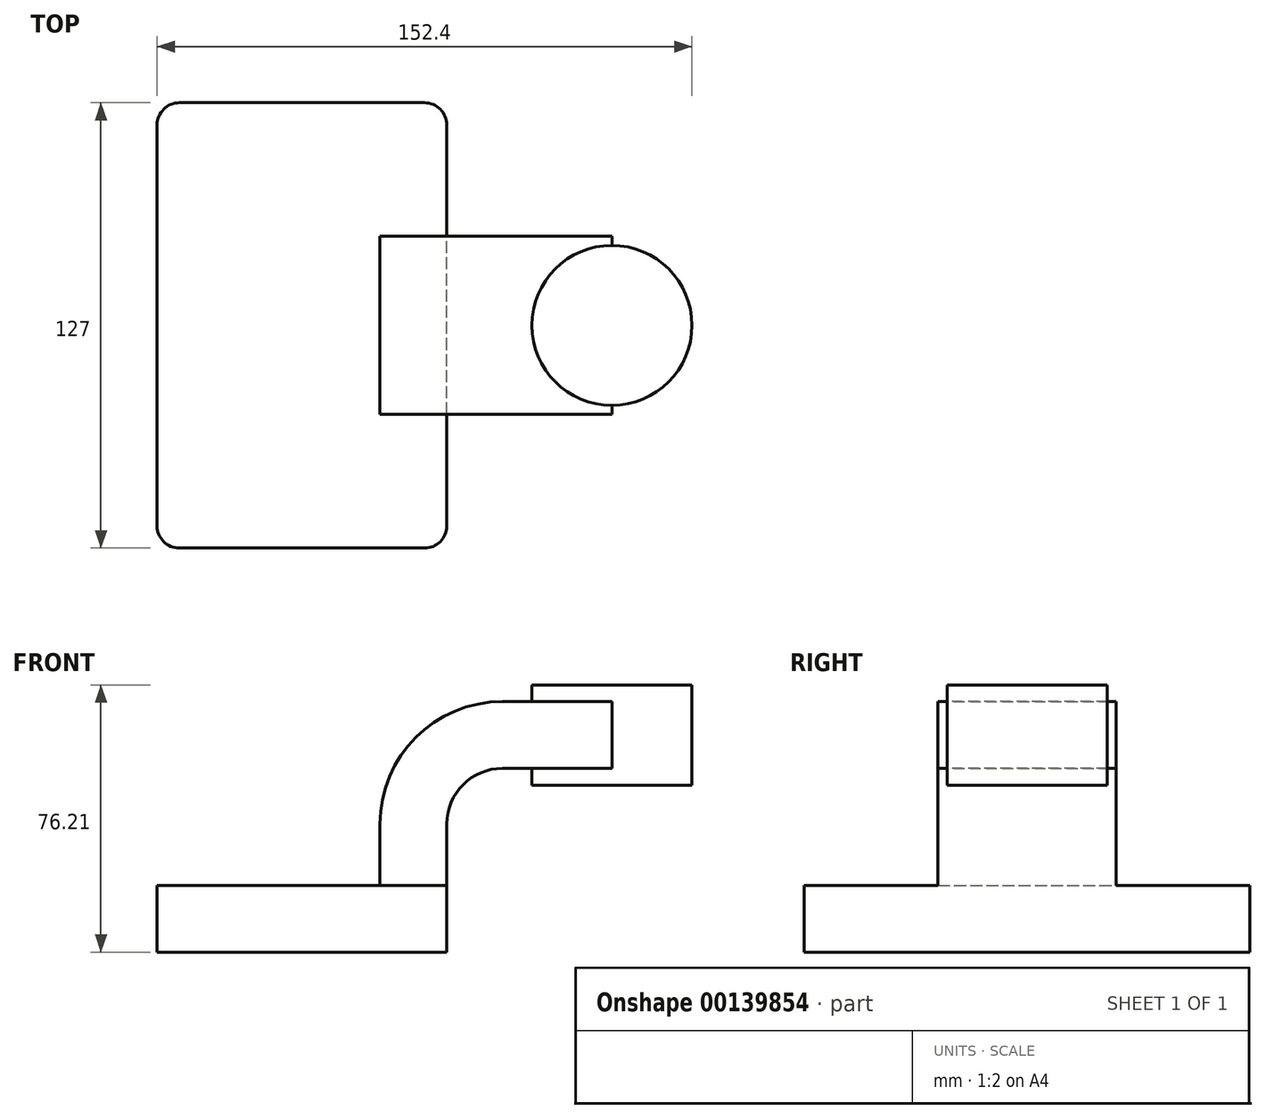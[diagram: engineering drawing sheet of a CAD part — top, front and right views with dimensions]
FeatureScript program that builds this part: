
annotation { "Feature Type Name" : "Feature", "Feature Type Description" : "" }
export const myFeature = defineFeature(function(context is Context, id is Id, definition is map)
    precondition{}
    {
        {
            var Q0;
            Q0=qCreatedBy(makeId("Front.planeOp"),FACE);
            var sketch = newSketch(context, id + "F0", { "sketchPlane" : qUnion([Q0])});
            skLineSegment(sketch, "E0.bottom", {"start": v(-41.28, 9.52) * mm, "end": v(41.27, 9.53) * mm});
            skLineSegment(sketch, "E0.top", {"start": v(-41.28, -9.53) * mm, "end": v(41.28, -9.53) * mm});
            skLineSegment(sketch, "E0.left", {"start": v(-41.28, 9.52) * mm, "end": v(-41.27, -9.53) * mm});
            skLineSegment(sketch, "E0.right", {"start": v(41.28, 9.53) * mm, "end": v(41.28, -9.52) * mm});
            skPoint(sketch, "E0.middle", {"position": v(0, 0) * mm});
            skLineSegment(sketch, "E1.bottom", {"start": v(111.12, 38.1) * mm, "end": v(60.32, 38.1) * mm});
            skLineSegment(sketch, "E1.top", {"start": v(111.12, 66.67) * mm, "end": v(60.32, 66.67) * mm});
            skLineSegment(sketch, "E1.left", {"start": v(111.12, 38.1) * mm, "end": v(111.12, 66.68) * mm});
            skLineSegment(sketch, "E1.right", {"start": v(60.32, 38.1) * mm, "end": v(60.32, 66.68) * mm});
            skPoint(sketch, "E1.middle", {"position": v(85.72, 52.39) * mm});
            skLineSegment(sketch, "E2", {"start": v(41.27, 9.53) * mm, "end": v(41.27, 27) * mm});
            skArc(sketch, "E3", {"start": v(41.27, 27) * mm, "mid": v(45.92, 38.23) * mm, "end": v(57.15, 42.88) * mm});
            skLineSegment(sketch, "E4", {"start": v(57.15, 42.88) * mm, "end": v(88.31, 42.88) * mm});
            skLineSegment(sketch, "E5.0", {"start": v(57.15, 61.93) * mm, "end": v(88.31, 61.93) * mm});
            skArc(sketch, "E5.1", {"start": v(22.22, 27) * mm, "mid": v(32.45, 51.7) * mm, "end": v(57.15, 61.93) * mm});
            skLineSegment(sketch, "E5.2", {"start": v(22.23, 9.53) * mm, "end": v(22.23, 27) * mm});
            skLineSegment(sketch, "E6", {"start": v(88.31, 42.88) * mm, "end": v(88.31, 66.67) * mm});
            skFitSpline(sketch, "E7", {"points": [v(-41.28, 9.53) * mm, v(60.32, 61.93) * mm], "startDerivative": vector(8.34, 87.8) * mm, "endDerivative": vector(60.06, -29.31) * mm});
            skLineSegment(sketch, "E8", {"start": v(88.31, 42.88) * mm, "end": v(88.31, 38.1) * mm});
            skSolve(sketch);
        }
        {
            var Q0;
            Q0=makeQuery(id+"F0.imprint","IMPRINT",FACE,{"disambiguationData":[TD([[makeQuery(id+"F0.imprint","IMPRINT",EDGE,{"derivedFrom":sQuery(id+"F0.wireOp",EDGE,"E0.top")}),1.0]])]});
            extrude(context, id + "F1", {"entities" : qUnion([Q0]), "endBound" : BoundingType.SYMMETRIC, "depth" : 127 * mm});
        }
        {
            var Q0;
            {var subQ1=sQuery(id+"F0.wireOp",EDGE,"E2");Q0=makeQuery(id+"F0.imprint","IMPRINT",FACE,{"disambiguationData":[TD([[makeQuery(id+"F0.imprint","IMPRINT",EDGE,{"derivedFrom":subQ1}),1.0]])]});}
            var Q1;
            {var subQ3=sQuery(id+"F0.wireOp",EDGE,"E4");var subQ5=sQuery(id+"F0.wireOp",EDGE,"E6");var subQ6=makeQuery(id+"F0.imprint","INTERSECT",VERTEX,{"derivedFrom":[subQ3,subQ5]});Q1=makeQuery(id+"F0.imprint","IMPRINT",FACE,{"disambiguationData":[TD([[makeQuery(id+"F0.imprint","IMPRINT",EDGE,{"disambiguationData":[TD([[subQ6,1.0]])],"derivedFrom":subQ3}),1.0]])]});}
            extrude(context, id + "F2", {"entities" : qUnion([Q0, Q1]), "operationType" : NewBodyOperationType.ADD, "endBound" : BoundingType.SYMMETRIC, "depth" : 50.8 * mm});
        }
        {
            var Q0;
            {var subQ1=sQuery(id+"F0.wireOp",EDGE,"E5.1");Q0=makeQuery(id+"F0.imprint","IMPRINT",FACE,{"disambiguationData":[TD([[makeQuery(id+"F0.imprint","IMPRINT",EDGE,{"derivedFrom":subQ1}),1.0]])]});}
            extrude(context, id + "F3", {"entities" : qUnion([Q0]), "operationType" : NewBodyOperationType.ADD, "endBound" : BoundingType.SYMMETRIC, "depth" : 15.88 * mm});
        }
        {
            var Q0;
            {var subQ0=sQuery(id+"F0.wireOp",EDGE,"E1.left");Q0=makeQuery(id+"F0.imprint","IMPRINT",FACE,{"disambiguationData":[TD([[makeQuery(id+"F0.imprint","IMPRINT",EDGE,{"derivedFrom":subQ0}),1.0]])]});}
            var Q1;
            Q1=sQuery(id+"F0.wireOp",EDGE,"E6");
            revolve(context, id + "F4", {"operationType" : NewBodyOperationType.ADD, "entities" : qUnion([Q0]), "axis" : qUnion([Q1]), "revolveType" : RevolveType.FULL});
        }
        {
            var Q0;
            Q0=makeQuery(id+"F1.opExtrude","CAP_EDGE",EDGE,{"disambiguationData":[OSD([sQuery(id+"F0.wireOp",EDGE,"E0.left")])],"isStart":false});
            var Q1;
            Q1=makeQuery(id+"F1.opExtrude","CAP_EDGE",EDGE,{"disambiguationData":[OSD([sQuery(id+"F0.wireOp",EDGE,"E0.right")])],"isStart":false});
            var Q2;
            Q2=makeQuery(id+"F1.opExtrude","CAP_EDGE",EDGE,{"disambiguationData":[OSD([sQuery(id+"F0.wireOp",EDGE,"E0.left")])],"isStart":true});
            var Q3;
            Q3=makeQuery(id+"F1.opExtrude","CAP_EDGE",EDGE,{"disambiguationData":[OSD([sQuery(id+"F0.wireOp",EDGE,"E0.right")])],"isStart":true});
            fillet(context, id + "F5", {"entities" : qUnion([Q0, Q1, Q2, Q3]), "radius" : 6.35 * mm, "tangentPropagation" : true, "allowEdgeOverflow" : false});
        }
    });
